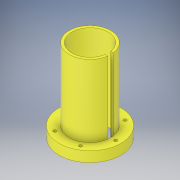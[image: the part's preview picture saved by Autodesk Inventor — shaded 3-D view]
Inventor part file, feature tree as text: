
AUTODESK INVENTOR PART (.ipt)
format: ipt  version: 2019.3 (Build 233278000, 278)  size: 162,816 bytes
history: native  units: in
note: dims shown in document units (in); Inventor stores cm internally (conversion verified against a paired STEP export)
features: sketch x5, extrude x4, hole x1
ambient origin geometry x8: Origin, YZ Plane, XZ Plane, XY Plane, X Axis, Y Axis, Z Axis, Center Point
bodies: Solid1 (feature_tree)
feature tree (10):
  extrude  "Extrusion1"  Depth=2.02in
  extrude  "Extrusion2"  Depth=0.27in
  extrude  "Extrusion3"  Depth=4.0in TaperAngle=0.0deg
  extrude  "Extrusion4"  Depth=3.0in
  hole  "Hole2"  [1 undecoded]
  sketch  "Sketch1"  dims[d0=1.77in d1=2.02in]
  sketch  "Sketch7"  dims[d2=4.0in d3=0.0in d10=0.27in]
  sketch  "Sketch8"  dims[d11=0.25in d12=4.0in d13=0.0in]
  sketch  "Sketch10"  dims[d14=2.02in d15=3.0in]
  sketch  "Sketch11"  dims[d16=0.5in d17=0.0in d30=0.191in d31=2.3622in d33=360.0deg d35=0.281in d36=0.0in d37=2.3622in d39=360.0deg d41=0.15in d42=0.75in d43=0.279in d44=0.25in d45=0.5635in d46=1.0in d47=0.8108in]
note: 1 required parameter value undecoded (feature->parameter linkage not recoverable at this tier; creation-order binding heuristic only, values carry confidence <= 0.55)
